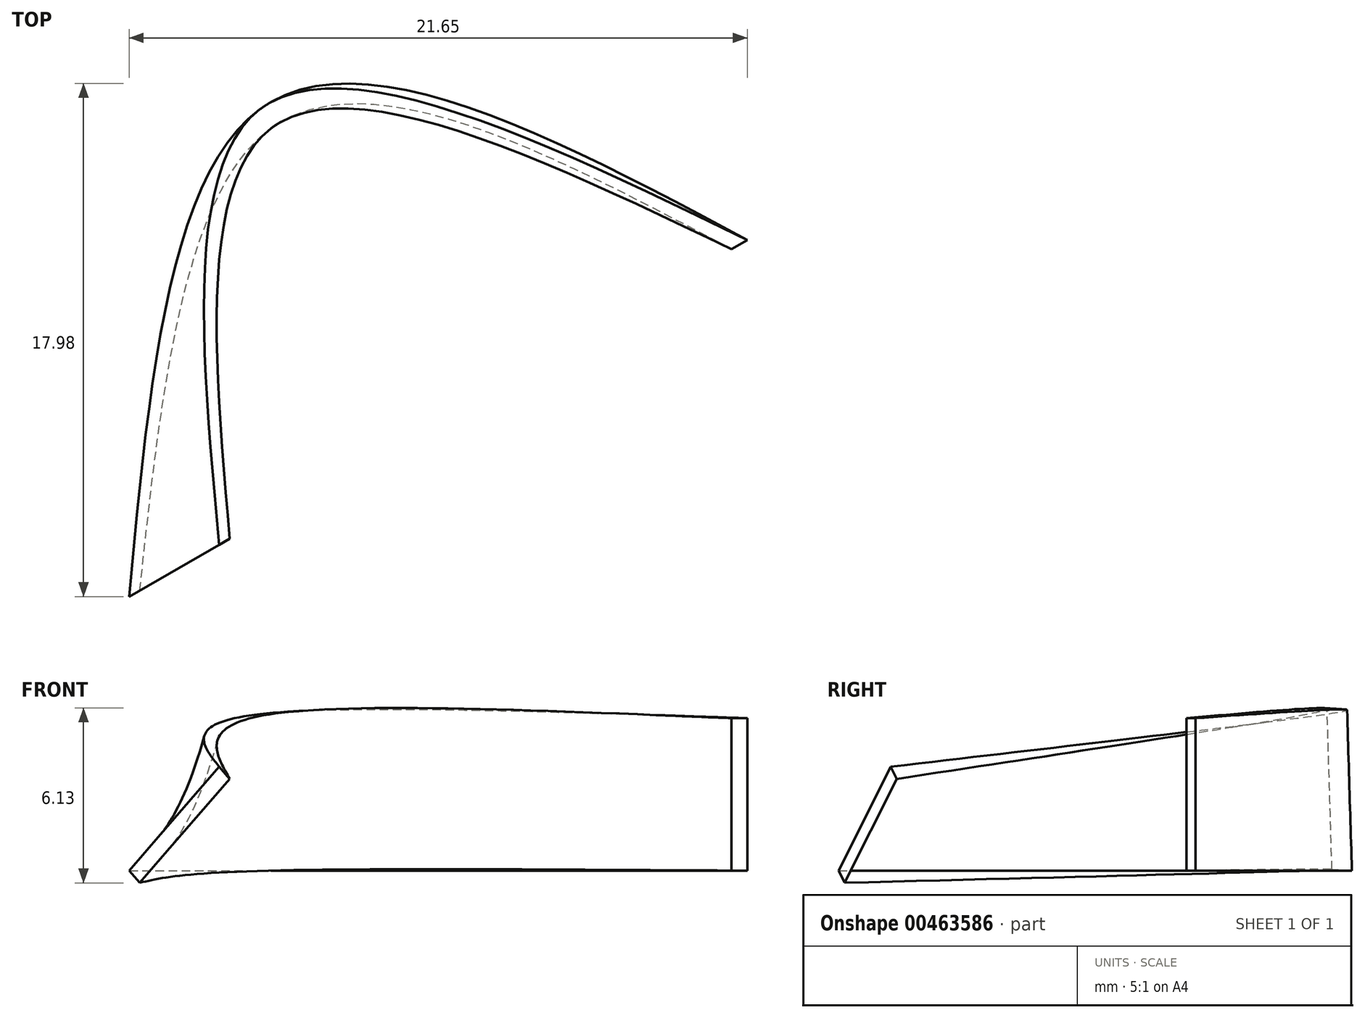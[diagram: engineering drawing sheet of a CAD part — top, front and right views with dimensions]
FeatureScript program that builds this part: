
annotation { "Feature Type Name" : "Feature", "Feature Type Description" : "" }
export const myFeature = defineFeature(function(context is Context, id is Id, definition is map)
    precondition{}
    {
        {
            var Q0;
            Q0=qCreatedBy(makeId("Top.planeOp"),FACE);
            var sketch = newSketch(context, id + "F0", { "sketchPlane" : qUnion([Q0])});
            skCircle(sketch, "E0", {"center": v(0, 0) * mm, "radius": 25 * mm});
            skCircle(sketch, "E1", {"center": v(0, 0) * mm, "radius": 1.5 * mm});
            skLineSegment(sketch, "E2", {"start": v(0, 0) * mm, "end": v(21.65, 12.5) * mm, "construction": true});
            skLineSegment(sketch, "E3", {"start": v(0, 0) * mm, "end": v(0, 25) * mm, "construction": true});
            skArc(sketch, "E4", {"start": v(21.65, 12.5) * mm, "mid": v(4.58, 17.08) * mm, "end": v(0, 0) * mm, "construction": true});
            skLineSegment(sketch, "E5", {"start": v(4.58, 17.08) * mm, "end": v(10.83, 6.25) * mm, "construction": true});
            skSolve(sketch);
        }
        {
            var Q0;
            Q0=sQuery(id+"F0.wireOp",EDGE,"E4");
            cPoint(context, id + "F1", {"entities" : qUnion([Q0]), "parameter" : 0.5});
        }
        {
            var Q0;
            Q0 = qCreatedBy(id + "F1" ,VERTEX);
            var Q1;
            Q1=sQuery(id+"F0.wireOp",EDGE,"E4");
            cPlane(context, id + "F2", {"entities" : qUnion([Q0, Q1]), "cplaneType" : CPlaneType.CURVE_POINT, "offset" : 25 * mm, "width" : 150 * mm, "height" : 150 * mm});
        }
        {
            var Q0;
            Q0=sQuery(id+"F0.wireOp",VERTEX,"E1.center");
            var Q1;
            Q1=sQuery(id+"F0.wireOp",EDGE,"E4");
            cPlane(context, id + "F3", {"entities" : qUnion([Q0, Q1]), "cplaneType" : CPlaneType.CURVE_POINT, "offset" : 25 * mm, "width" : 150 * mm, "height" : 150 * mm});
        }
        {
            var Q0;
            Q0=qCreatedBy(id+"F3.planeOp",FACE);
            var sketch = newSketch(context, id + "F4", { "sketchPlane" : qUnion([Q0])});
            skLineSegment(sketch, "E6.0", {"start": v(0, 0) * mm, "end": v(25, 0) * mm, "construction": true});
            skLineSegment(sketch, "E7.bottom", {"start": v(0, 0) * mm, "end": v(0.43, -0.43) * mm});
            skLineSegment(sketch, "E7.top", {"start": v(3.64, 3.64) * mm, "end": v(4.07, 3.21) * mm});
            skLineSegment(sketch, "E7.left", {"start": v(0, 0) * mm, "end": v(3.64, 3.64) * mm});
            skLineSegment(sketch, "E7.right", {"start": v(0.43, -0.43) * mm, "end": v(4.07, 3.21) * mm});
            skLineSegment(sketch, "E8.bottom", {"start": v(25, 0) * mm, "end": v(24.36, 0) * mm});
            skLineSegment(sketch, "E8.top", {"start": v(25, 5.34) * mm, "end": v(24.36, 5.34) * mm});
            skLineSegment(sketch, "E8.left", {"start": v(25, 0) * mm, "end": v(25, 5.34) * mm});
            skLineSegment(sketch, "E8.right", {"start": v(24.36, 0) * mm, "end": v(24.36, 5.34) * mm});
            skSolve(sketch);
        }
        {
            var Q0;
            Q0=qCreatedBy(id+"F2.planeOp",FACE);
            var sketch = newSketch(context, id + "F5", { "sketchPlane" : qUnion([Q0])});
            skLineSegment(sketch, "E9.0", {"start": v(-12.5, 0) * mm, "end": v(0, 0) * mm, "construction": true});
            skLineSegment(sketch, "E10.bottom", {"start": v(-12.5, 0) * mm, "end": v(-11.73, 0) * mm});
            skLineSegment(sketch, "E10.top", {"start": v(-12.5, 5.48) * mm, "end": v(-11.73, 5.48) * mm});
            skLineSegment(sketch, "E10.left", {"start": v(-12.5, 0) * mm, "end": v(-12.5, 5.48) * mm});
            skLineSegment(sketch, "E10.right", {"start": v(-11.73, 0) * mm, "end": v(-11.73, 5.48) * mm});
            skSolve(sketch);
        }
        {
            var Q0;
            Q0=makeQuery(id+"F4.imprint","IMPRINT",FACE,{"disambiguationData":[TD([[makeQuery(id+"F4.imprint","IMPRINT",EDGE,{"derivedFrom":sQuery(id+"F4.wireOp",EDGE,"E7.bottom")}),1.0]])]});
            var Q1;
            Q1=makeQuery(id+"F5.imprint","IMPRINT",FACE,{"disambiguationData":[TD([[makeQuery(id+"F5.imprint","IMPRINT",EDGE,{"derivedFrom":sQuery(id+"F5.wireOp",EDGE,"E10.bottom")}),1.0]])]});
            var Q2;
            Q2=makeQuery(id+"F4.imprint","IMPRINT",FACE,{"disambiguationData":[TD([[makeQuery(id+"F4.imprint","IMPRINT",EDGE,{"derivedFrom":sQuery(id+"F4.wireOp",EDGE,"E8.bottom")}),-1.0]])]});
            loft(context, id + "F6", {"sheetProfilesArray" : [{ "sheetProfileEntities" : qUnion([Q0]) }, { "sheetProfileEntities" : qUnion([Q1]) }, { "sheetProfileEntities" : qUnion([Q2]) }]});
        }
    });
